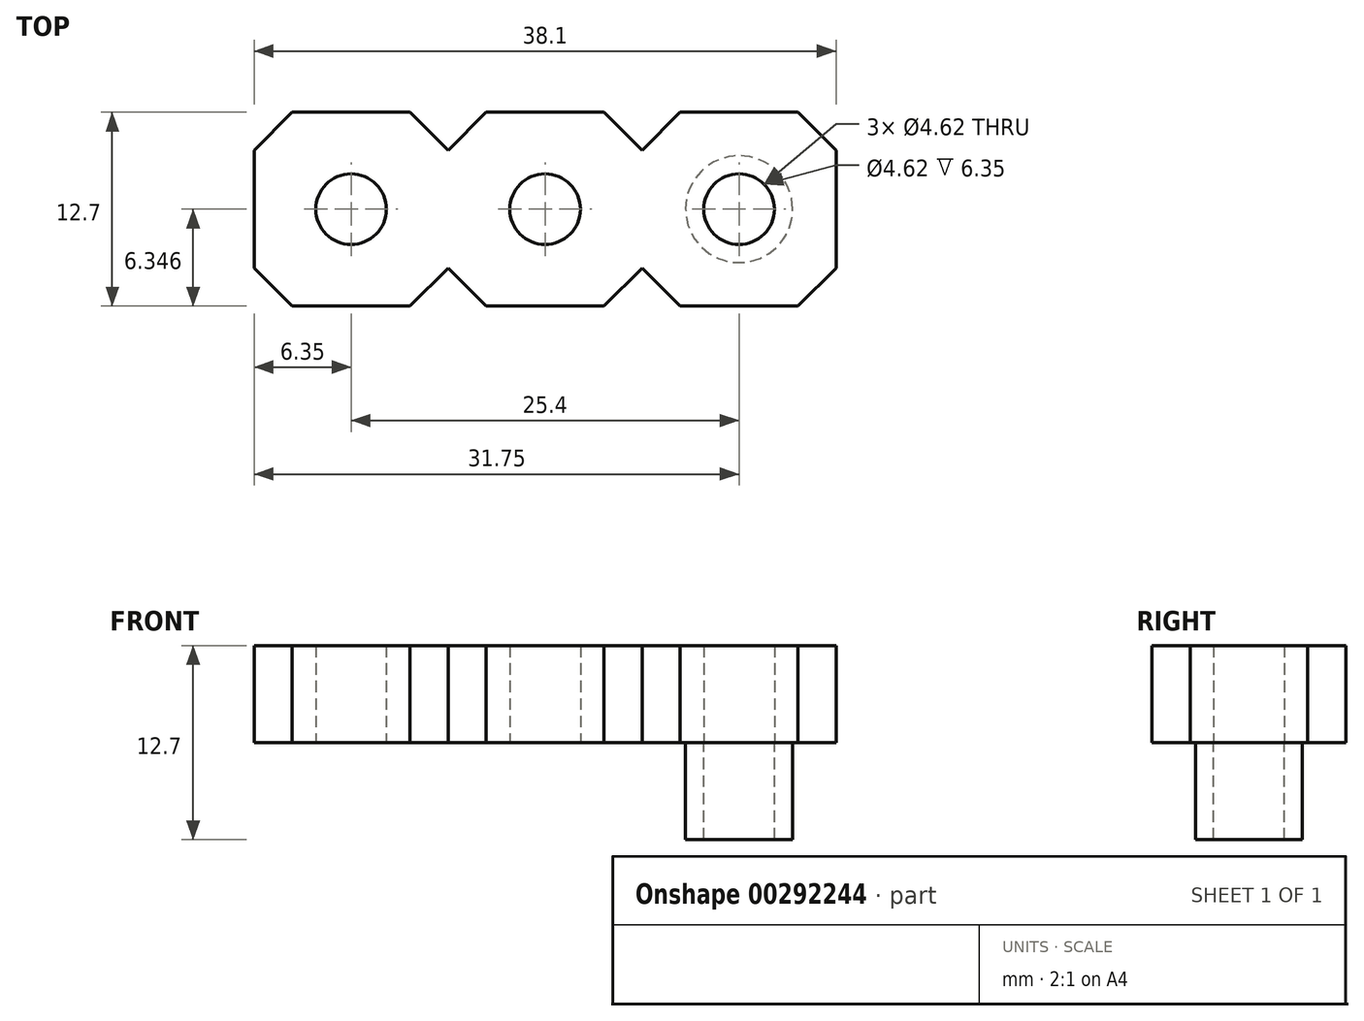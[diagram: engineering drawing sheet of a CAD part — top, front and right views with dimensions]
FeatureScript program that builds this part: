
annotation { "Feature Type Name" : "Feature", "Feature Type Description" : "" }
export const myFeature = defineFeature(function(context is Context, id is Id, definition is map)
    precondition{}
    {
        {
            var Q0;
            Q0=qCreatedBy(makeId("Top.planeOp"),FACE);
            var sketch = newSketch(context, id + "F0", { "sketchPlane" : qUnion([Q0])});
            skLineSegment(sketch, "E0.bottom", {"start": v(19.05, -5.8) * mm, "end": v(-19.05, -5.8) * mm});
            skLineSegment(sketch, "E0.top", {"start": v(19.05, 6.9) * mm, "end": v(-19.05, 6.9) * mm});
            skLineSegment(sketch, "E0.left", {"start": v(19.05, -5.8) * mm, "end": v(19.05, 6.9) * mm});
            skLineSegment(sketch, "E0.right", {"start": v(-19.05, -5.8) * mm, "end": v(-19.05, 6.9) * mm});
            skPoint(sketch, "E0.middle", {"position": v(0, 0.56) * mm});
            skLineSegment(sketch, "E1", {"start": v(-19.05, 0.56) * mm, "end": v(0, 0.56) * mm});
            skLineSegment(sketch, "E2", {"start": v(0, 0.56) * mm, "end": v(19.05, 0.56) * mm});
            skCircle(sketch, "E3", {"center": v(0, 0.56) * mm, "radius": 2.31 * mm});
            skLineSegment(sketch, "E4", {"start": v(0, 0.56) * mm, "end": v(-12.7, 0.56) * mm});
            skCircle(sketch, "E5", {"center": v(-12.7, 0.56) * mm, "radius": 2.31 * mm});
            skLineSegment(sketch, "E6", {"start": v(0, 0.56) * mm, "end": v(12.7, 0.56) * mm});
            skCircle(sketch, "E7", {"center": v(12.7, 0.56) * mm, "radius": 2.31 * mm});
            skLineSegment(sketch, "E8", {"start": v(6.35, 6.9) * mm, "end": v(6.35, -5.8) * mm});
            skPoint(sketch, "E8.startSnap0", {"position": v(6.35, 0.56) * mm});
            skLineSegment(sketch, "E9", {"start": v(6.35, -5.8) * mm, "end": v(-6.35, -5.8) * mm});
            skPoint(sketch, "E9.endSnap0", {"position": v(-6.35, 0.56) * mm});
            skLineSegment(sketch, "E10", {"start": v(-6.35, -5.8) * mm, "end": v(-6.35, 6.9) * mm});
            skLineSegment(sketch, "E11", {"start": v(-6.35, 6.9) * mm, "end": v(-8.85, 6.9) * mm});
            skLineSegment(sketch, "E12", {"start": v(-8.85, 6.9) * mm, "end": v(-6.35, 4.4) * mm});
            skLineSegment(sketch, "E13.MirrorCS", {"start": v(-3.85, 6.9) * mm, "end": v(-6.35, 4.4) * mm});
            skLineSegment(sketch, "E14.1.0.0", {"start": v(8.85, 6.9) * mm, "end": v(6.35, 4.4) * mm});
            skLineSegment(sketch, "E14.1.0.1", {"start": v(3.85, 6.9) * mm, "end": v(6.35, 4.4) * mm});
            skLineSegment(sketch, "E14.direction1", {"start": v(-6.35, 4.4) * mm, "end": v(6.35, 4.4) * mm, "construction": true});
            skLineSegment(sketch, "E15.MirrorCS", {"start": v(-3.85, -5.8) * mm, "end": v(-6.35, -3.3) * mm});
            skLineSegment(sketch, "E16.MirrorCS", {"start": v(-8.85, -5.8) * mm, "end": v(-6.35, -3.3) * mm});
            skLineSegment(sketch, "E17.MirrorCS", {"start": v(3.85, -5.8) * mm, "end": v(6.35, -3.3) * mm});
            skLineSegment(sketch, "E18.MirrorCS", {"start": v(8.85, -5.8) * mm, "end": v(6.35, -3.3) * mm});
            skLineSegment(sketch, "E19.MirrorCS", {"start": v(16.55, 6.9) * mm, "end": v(19.05, 4.4) * mm});
            skLineSegment(sketch, "E20.MirrorCS", {"start": v(16.55, -5.8) * mm, "end": v(19.05, -3.3) * mm});
            skLineSegment(sketch, "E21.MirrorCS", {"start": v(-16.55, 6.9) * mm, "end": v(-19.05, 4.4) * mm});
            skLineSegment(sketch, "E22.MirrorCS", {"start": v(-16.55, -5.8) * mm, "end": v(-19.05, -3.3) * mm});
            skSolve(sketch);
        }
        {
            var Q0;
            {var subQ5=sQuery(id+"F0.wireOp",EDGE,"E12");Q0=makeQuery(id+"F0.imprint","IMPRINT",FACE,{"disambiguationData":[TD([[makeQuery(id+"F0.imprint","IMPRINT",EDGE,{"derivedFrom":subQ5}),-1.0]])]});}
            var Q1;
            {var subQ10=sQuery(id+"F0.wireOp",EDGE,"E16.MirrorCS");Q1=makeQuery(id+"F0.imprint","IMPRINT",FACE,{"disambiguationData":[TD([[makeQuery(id+"F0.imprint","IMPRINT",EDGE,{"derivedFrom":subQ10}),1.0]])]});}
            var Q2;
            {var subQ10=sQuery(id+"F0.wireOp",EDGE,"E15.MirrorCS");Q2=makeQuery(id+"F0.imprint","IMPRINT",FACE,{"disambiguationData":[TD([[makeQuery(id+"F0.imprint","IMPRINT",EDGE,{"derivedFrom":subQ10}),-1.0]])]});}
            var Q3;
            {var subQ9=sQuery(id+"F0.wireOp",EDGE,"E13.MirrorCS");Q3=makeQuery(id+"F0.imprint","IMPRINT",FACE,{"disambiguationData":[TD([[makeQuery(id+"F0.imprint","IMPRINT",EDGE,{"derivedFrom":subQ9}),1.0]])]});}
            var Q4;
            {var subQ10=sQuery(id+"F0.wireOp",EDGE,"E14.1.0.0");Q4=makeQuery(id+"F0.imprint","IMPRINT",FACE,{"disambiguationData":[TD([[makeQuery(id+"F0.imprint","IMPRINT",EDGE,{"derivedFrom":subQ10}),1.0]])]});}
            var Q5;
            {var subQ10=sQuery(id+"F0.wireOp",EDGE,"E18.MirrorCS");Q5=makeQuery(id+"F0.imprint","IMPRINT",FACE,{"disambiguationData":[TD([[makeQuery(id+"F0.imprint","IMPRINT",EDGE,{"derivedFrom":subQ10}),-1.0]])]});}
            extrude(context, id + "F1", {"entities" : qUnion([Q0, Q1, Q2, Q3, Q4, Q5]), "depth" : 6.35 * mm});
        }
        {
            var Q0;
            Q0=makeQuery(id+"F1.opExtrude","CAP_FACE",FACE,{"disambiguationData":[OSD([sQuery(id+"F0.wireOp",EDGE,"E0.bottom"),sQuery(id+"F0.wireOp",EDGE,"E0.top"),sQuery(id+"F0.wireOp",EDGE,"E0.left"),sQuery(id+"F0.wireOp",EDGE,"E0.right"),sQuery(id+"F0.wireOp",EDGE,"E3"),sQuery(id+"F0.wireOp",EDGE,"E5"),sQuery(id+"F0.wireOp",EDGE,"E7"),sQuery(id+"F0.wireOp",EDGE,"E9"),sQuery(id+"F0.wireOp",EDGE,"E12"),sQuery(id+"F0.wireOp",EDGE,"E13.MirrorCS"),sQuery(id+"F0.wireOp",EDGE,"E14.1.0.0"),sQuery(id+"F0.wireOp",EDGE,"E14.1.0.1"),sQuery(id+"F0.wireOp",EDGE,"E15.MirrorCS"),sQuery(id+"F0.wireOp",EDGE,"E16.MirrorCS"),sQuery(id+"F0.wireOp",EDGE,"E17.MirrorCS"),sQuery(id+"F0.wireOp",EDGE,"E18.MirrorCS"),sQuery(id+"F0.wireOp",EDGE,"E19.MirrorCS"),sQuery(id+"F0.wireOp",EDGE,"E20.MirrorCS"),sQuery(id+"F0.wireOp",EDGE,"E21.MirrorCS"),sQuery(id+"F0.wireOp",EDGE,"E22.MirrorCS")])],"isStart":true});
            var sketch = newSketch(context, id + "F2", { "sketchPlane" : qUnion([Q0])});
            skCircle(sketch, "E23", {"center": v(12.7, -0.56) * mm, "radius": 2.31 * mm});
            skCircle(sketch, "E24", {"center": v(12.7, -0.56) * mm, "radius": 3.5 * mm});
            skSolve(sketch);
        }
        {
            var Q0;
            Q0 = qSketchRegion(id + "F2", true);
            extrude(context, id + "F3", {"entities" : qUnion([Q0]), "depth" : 6.35 * mm});
        }
    });
